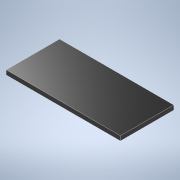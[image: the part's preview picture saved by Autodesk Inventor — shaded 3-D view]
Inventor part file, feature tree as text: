
AUTODESK INVENTOR PART (.ipt)
format: ipt  version: 2021 (Build 250183000, 183)  size: 94,720 bytes
history: native  units: mm
features: extrude x1, sketch x1
ambient origin geometry x8: Origin, YZ Plane, XZ Plane, XY Plane, X Axis, Y Axis, Z Axis, Center Point
bodies: Solid1 (feature_tree)
feature tree (2):
  extrude  "Extrusion1"  Depth=120.0mm
  sketch  "Sketch1"  dims[d0=257.0mm d1=120.0mm d2=10.0mm d3=0.0mm]
